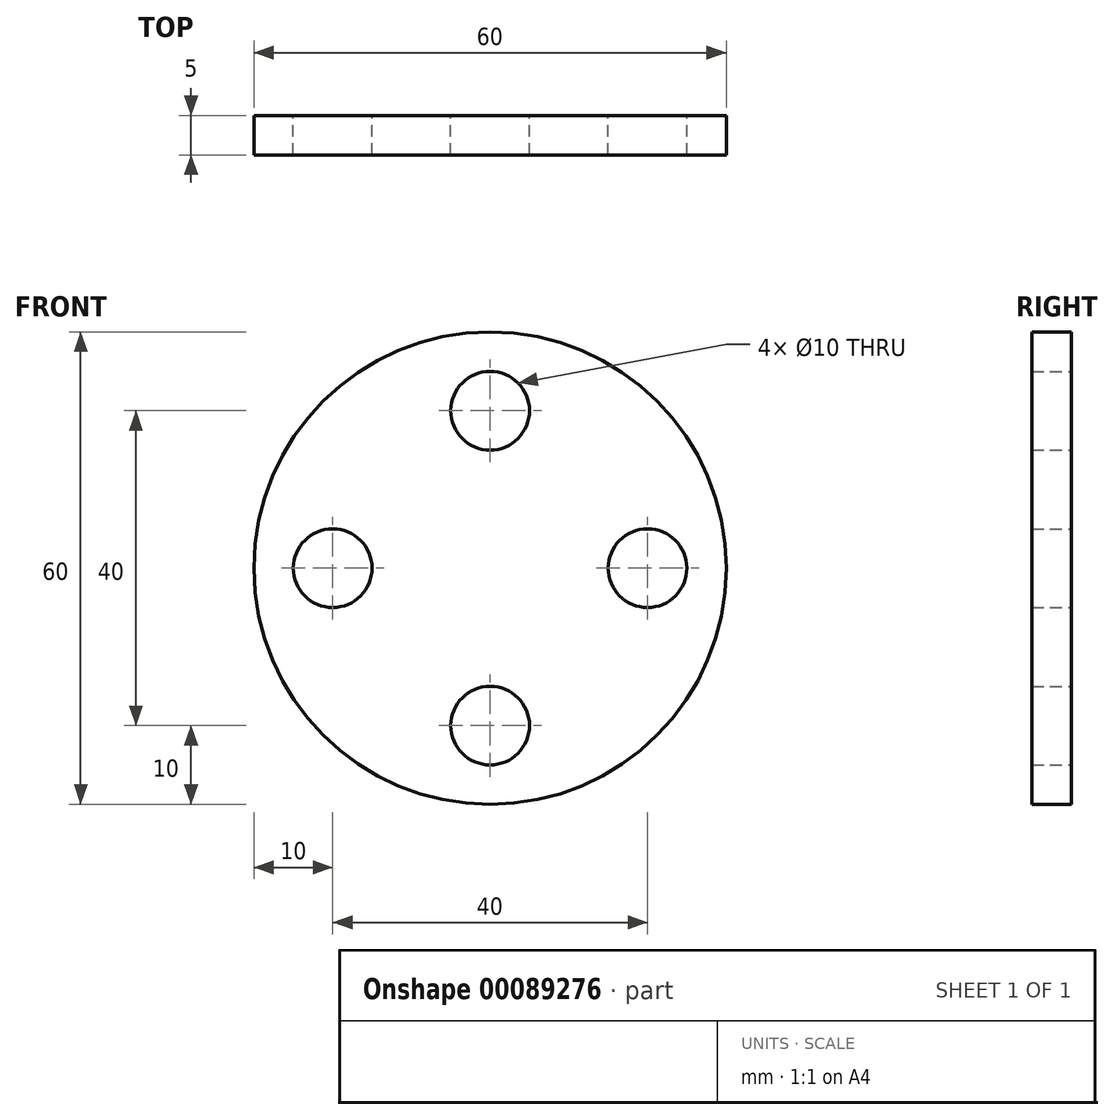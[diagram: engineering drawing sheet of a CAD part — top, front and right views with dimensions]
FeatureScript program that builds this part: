
annotation { "Feature Type Name" : "Feature", "Feature Type Description" : "" }
export const myFeature = defineFeature(function(context is Context, id is Id, definition is map)
    precondition{}
    {
        {
            var Q0;
            Q0=qCreatedBy(makeId("Front.planeOp"),FACE);
            var sketch = newSketch(context, id + "F0", { "sketchPlane" : qUnion([Q0])});
            skCircle(sketch, "E0", {"center": v(0, 0) * mm, "radius": 30 * mm});
            skCircle(sketch, "E1", {"center": v(0, 0) * mm, "radius": 20 * mm, "construction": true});
            skLineSegment(sketch, "E2", {"start": v(-30, 0) * mm, "end": v(30, 0) * mm, "construction": true});
            skLineSegment(sketch, "E3", {"start": v(0, -30) * mm, "end": v(0, 30) * mm, "construction": true});
            skCircle(sketch, "E4", {"center": v(-20, 0) * mm, "radius": 5 * mm});
            skCircle(sketch, "E5.1.0", {"center": v(0, 20) * mm, "radius": 5 * mm});
            skCircle(sketch, "E5.2.0", {"center": v(20, 0) * mm, "radius": 5 * mm});
            skCircle(sketch, "E5.3.0", {"center": v(0, -20) * mm, "radius": 5 * mm});
            skLineSegment(sketch, "E5.anchor1", {"start": v(0, 0) * mm, "end": v(-20, 0) * mm, "construction": true});
            skLineSegment(sketch, "E5.anchor2", {"start": v(0, 0) * mm, "end": v(0, -20) * mm, "construction": true});
            skSolve(sketch);
        }
        {
            var Q0;
            Q0 = qSketchRegion(id + "F0", true);
            extrude(context, id + "F1", {"entities" : qUnion([Q0]), "depth" : 5 * mm});
        }
    });
